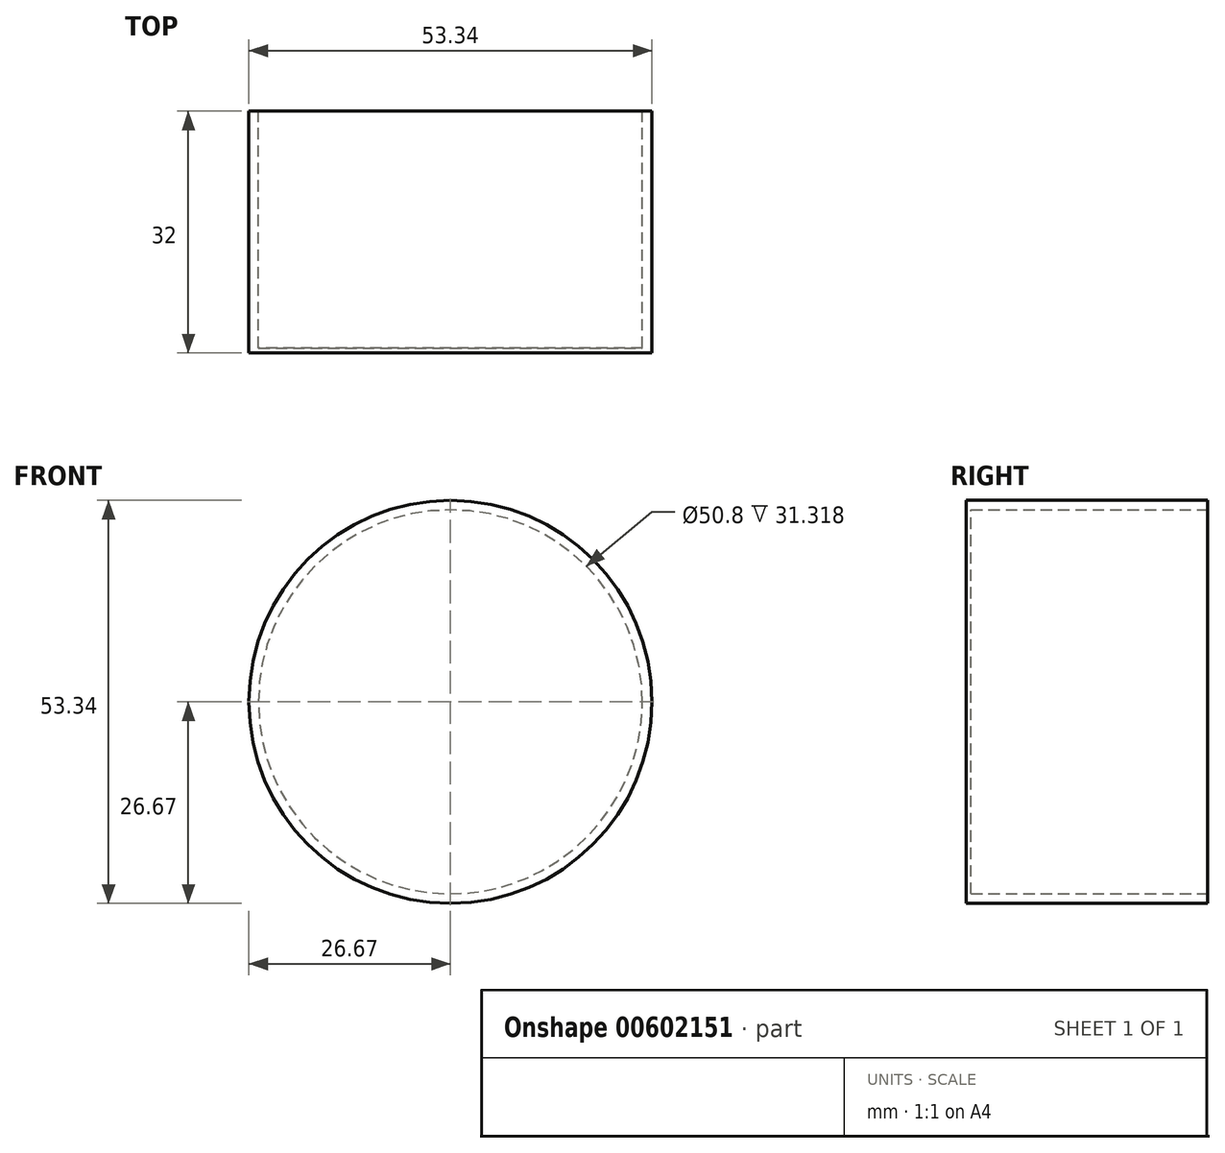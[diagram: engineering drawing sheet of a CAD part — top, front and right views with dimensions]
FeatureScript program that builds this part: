
annotation { "Feature Type Name" : "Feature", "Feature Type Description" : "" }
export const myFeature = defineFeature(function(context is Context, id is Id, definition is map)
    precondition{}
    {
        {
            var Q0;
            Q0=qCreatedBy(makeId("Front.planeOp"),FACE);
            var sketch = newSketch(context, id + "F0", { "sketchPlane" : qUnion([Q0])});
            skCircle(sketch, "E0", {"center": v(0, 0) * mm, "radius": 26.67 * mm});
            skSolve(sketch);
        }
        {
            var Q0;
            Q0=makeQuery(id+"F0.imprint","IMPRINT",FACE,{"disambiguationData":[TD([[makeQuery(id+"F0.imprint","IMPRINT",EDGE,{"derivedFrom":sQuery(id+"F0.wireOp",EDGE,"E0")}),1.0]])]});
            var sketch = newSketch(context, id + "F1", { "sketchPlane" : qUnion([Q0])});
            skCircle(sketch, "E1", {"center": v(0, 0) * mm, "radius": 25.4 * mm});
            skSolve(sketch);
        }
        {
            var Q0;
            Q0=makeQuery(id+"F0.imprint","IMPRINT",FACE,{"disambiguationData":[TD([[makeQuery(id+"F0.imprint","IMPRINT",EDGE,{"derivedFrom":sQuery(id+"F0.wireOp",EDGE,"E0")}),1.0]])]});
            var Q1;
            Q1=sQuery(id+"F0.wireOp",EDGE,"E0");
            var Q2;
            Q2=sQuery(id+"F1.wireOp",EDGE,"E1");
            extrude(context, id + "F2", {"entities" : qUnion([Q0]), "surfaceEntities" : qUnion([Q1, Q2]), "depth" : 32 * mm, "offsetDistance" : 25.4 * mm});
        }
        {
            var Q0;
            Q0 = qSketchRegion(id + "F1", true);
            extrude(context, id + "F3", {"entities" : qUnion([Q0]), "operationType" : NewBodyOperationType.REMOVE, "depth" : 31.32 * mm, "offsetDistance" : 25.4 * mm});
        }
    });
